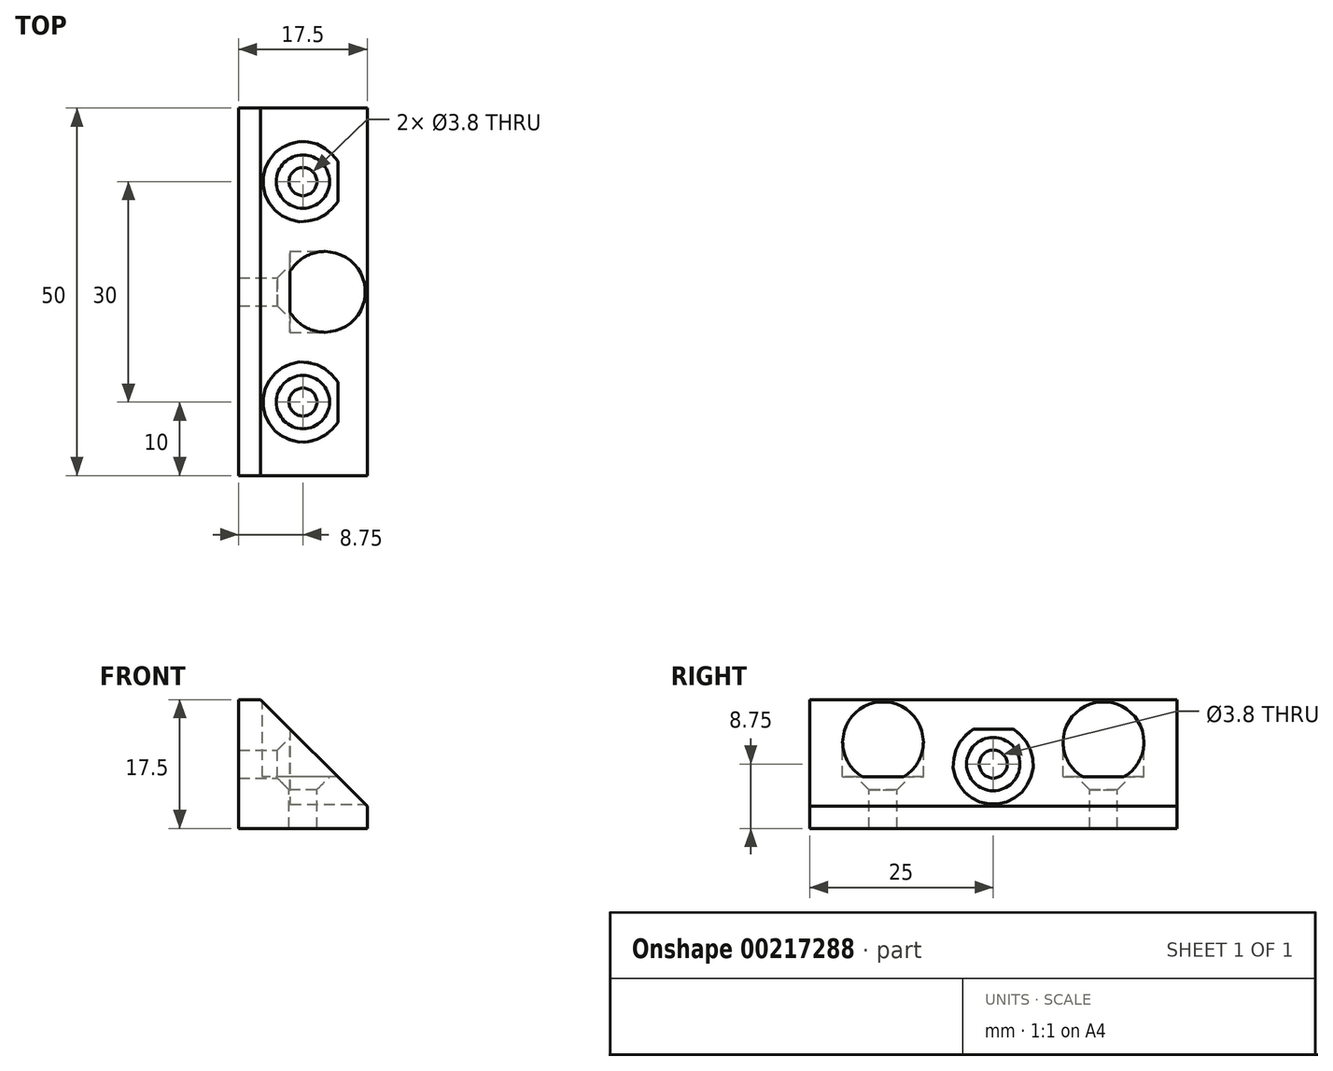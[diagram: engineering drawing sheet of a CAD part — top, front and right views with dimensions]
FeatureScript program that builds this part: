
annotation { "Feature Type Name" : "Feature", "Feature Type Description" : "" }
export const myFeature = defineFeature(function(context is Context, id is Id, definition is map)
    precondition{}
    {
        {
            var Q0;
            Q0=qCreatedBy(makeId("Front.planeOp"),FACE);
            var sketch = newSketch(context, id + "F0", { "sketchPlane" : qUnion([Q0])});
            skLineSegment(sketch, "E0", {"start": v(0, 17.5) * mm, "end": v(0, 0) * mm});
            skLineSegment(sketch, "E1", {"start": v(0, 0) * mm, "end": v(17.5, 0) * mm});
            skLineSegment(sketch, "E2", {"start": v(17.5, 0) * mm, "end": v(17.5, 3) * mm});
            skLineSegment(sketch, "E3", {"start": v(0, 17.5) * mm, "end": v(3, 17.5) * mm});
            skPoint(sketch, "E4.orphan", {"position": v(0, 20.42) * mm});
            skLineSegment(sketch, "E5", {"start": v(3, 17.5) * mm, "end": v(17.5, 3) * mm});
            skSolve(sketch);
        }
        {
            var Q0;
            Q0=makeQuery(id+"F0.imprint","IMPRINT",FACE,{"disambiguationData":[TD([[makeQuery(id+"F0.imprint","IMPRINT",EDGE,{"derivedFrom":sQuery(id+"F0.wireOp",EDGE,"E0")}),1.0]])]});
            extrude(context, id + "F1", {"entities" : qUnion([Q0]), "oppositeDirection" : true, "depth" : 50 * mm});
        }
        {
            var Q0;
            Q0=qCreatedBy(makeId("Top.planeOp"),FACE);
            cPlane(context, id + "F2", {"entities" : qUnion([Q0]), "cplaneType" : CPlaneType.OFFSET, "offset" : 17.5 * mm, "width" : 150 * mm, "height" : 150 * mm});
        }
        {
            var Q0;
            Q0=qCreatedBy(id+"F2.planeOp",FACE);
            var sketch = newSketch(context, id + "F3", { "sketchPlane" : qUnion([Q0])});
            skCircle(sketch, "E6", {"center": v(8.75, 10) * mm, "radius": 5.5 * mm});
            skCircle(sketch, "E7.0.1.0", {"center": v(8.75, 40) * mm, "radius": 5.5 * mm});
            skLineSegment(sketch, "E7.direction1", {"start": v(8.75, 10) * mm, "end": v(-11.25, 10) * mm, "construction": true});
            skLineSegment(sketch, "E7.direction2", {"start": v(8.75, 10) * mm, "end": v(8.75, 40) * mm, "construction": true});
            skSolve(sketch);
        }
        {
            var Q0;
            Q0=makeQuery(id+"F3.imprint","IMPRINT",FACE,{"disambiguationData":[TD([[makeQuery(id+"F3.imprint","IMPRINT",EDGE,{"derivedFrom":sQuery(id+"F3.wireOp",EDGE,"E7.0.1.0")}),1.0]])]});
            var Q1;
            Q1=makeQuery(id+"F3.imprint","IMPRINT",FACE,{"disambiguationData":[TD([[makeQuery(id+"F3.imprint","IMPRINT",EDGE,{"derivedFrom":sQuery(id+"F3.wireOp",EDGE,"E6")}),1.0]])]});
            extrude(context, id + "F4", {"entities" : qUnion([Q0, Q1]), "operationType" : NewBodyOperationType.REMOVE, "oppositeDirection" : true, "depth" : 10.5 * mm});
        }
        {
            var Q0;
            Q0=qCreatedBy(makeId("Right.planeOp"),FACE);
            cPlane(context, id + "F5", {"entities" : qUnion([Q0]), "cplaneType" : CPlaneType.OFFSET, "offset" : 17.5 * mm, "width" : 150 * mm, "height" : 150 * mm});
        }
        {
            var Q0;
            Q0=qCreatedBy(id+"F5.planeOp",FACE);
            var sketch = newSketch(context, id + "F6", { "sketchPlane" : qUnion([Q0])});
            skCircle(sketch, "E8", {"center": v(25, 8.75) * mm, "radius": 5.5 * mm});
            skSolve(sketch);
        }
        {
            var Q0;
            Q0 = qSketchRegion(id + "F6", true);
            extrude(context, id + "F7", {"entities" : qUnion([Q0]), "operationType" : NewBodyOperationType.REMOVE, "oppositeDirection" : true, "depth" : 10.5 * mm});
        }
        {
            var Q0;
            Q0=makeQuery(id+"F4.boolean.opBoolean","COPY",FACE,{"derivedFrom":makeQuery(id+"F4.opExtrude","CAP_FACE",FACE,{"disambiguationData":[OSD([sQuery(id+"F3.wireOp",EDGE,"E7.0.1.0")])],"isStart":false})});
            var sketch = newSketch(context, id + "F8", { "sketchPlane" : qUnion([Q0])});
            skCircle(sketch, "E9.0", {"center": v(8.75, 40) * mm, "radius": 5.5 * mm});
            skCircle(sketch, "E10.0", {"center": v(8.75, 10) * mm, "radius": 5.5 * mm});
            skSolve(sketch);
        }
        {
            var Q0;
            Q0=sQuery(id+"F8.wireOp",VERTEX,"E9.0.center");
            var Q1;
            Q1=sQuery(id+"F8.wireOp",VERTEX,"E10.0.center");
            var Q2;
            Q2=makeQuery(id+"F1.opExtrude","SWEPT_BODY",BODY,{"disambiguationData":[OSD([sQuery(id+"F0.wireOp",EDGE,"E0"),sQuery(id+"F0.wireOp",EDGE,"E1"),sQuery(id+"F0.wireOp",EDGE,"E2"),sQuery(id+"F0.wireOp",EDGE,"E3"),sQuery(id+"F0.wireOp",EDGE,"E5")])]});
            hole(context, id + "F9", {"style" : HoleStyle.C_SINK, "endStyle" : HoleEndStyle.THROUGH, "holeDiameter" : 3.8 * mm, "cSinkDiameter" : 7.25 * mm, "cSinkAngle" : 90 * degree, "startFromSketch" : true, "locations" : qUnion([Q0, Q1]), "scope" : qUnion([Q2]), "isTappedThrough" : true});
        }
        {
            var Q0;
            Q0=makeQuery(id+"F7.boolean.opBoolean","COPY",FACE,{"derivedFrom":makeQuery(id+"F7.opExtrude","CAP_FACE",FACE,{"disambiguationData":[OSD([sQuery(id+"F6.wireOp",EDGE,"E8")])],"isStart":false})});
            var sketch = newSketch(context, id + "F10", { "sketchPlane" : qUnion([Q0])});
            skCircle(sketch, "E11.0", {"center": v(25, 8.75) * mm, "radius": 5.5 * mm});
            skSolve(sketch);
        }
        {
            var Q0;
            Q0=sQuery(id+"F10.wireOp",VERTEX,"E11.0.center");
            var Q1;
            Q1=makeQuery(id+"F1.opExtrude","SWEPT_BODY",BODY,{"disambiguationData":[OSD([sQuery(id+"F0.wireOp",EDGE,"E0"),sQuery(id+"F0.wireOp",EDGE,"E1"),sQuery(id+"F0.wireOp",EDGE,"E2"),sQuery(id+"F0.wireOp",EDGE,"E3"),sQuery(id+"F0.wireOp",EDGE,"E5")])]});
            hole(context, id + "F11", {"style" : HoleStyle.C_SINK, "endStyle" : HoleEndStyle.THROUGH, "holeDiameter" : 3.8 * mm, "cSinkDiameter" : 7.25 * mm, "cSinkAngle" : 90 * degree, "startFromSketch" : true, "locations" : qUnion([Q0]), "scope" : qUnion([Q1]), "isTappedThrough" : true});
        }
    });
